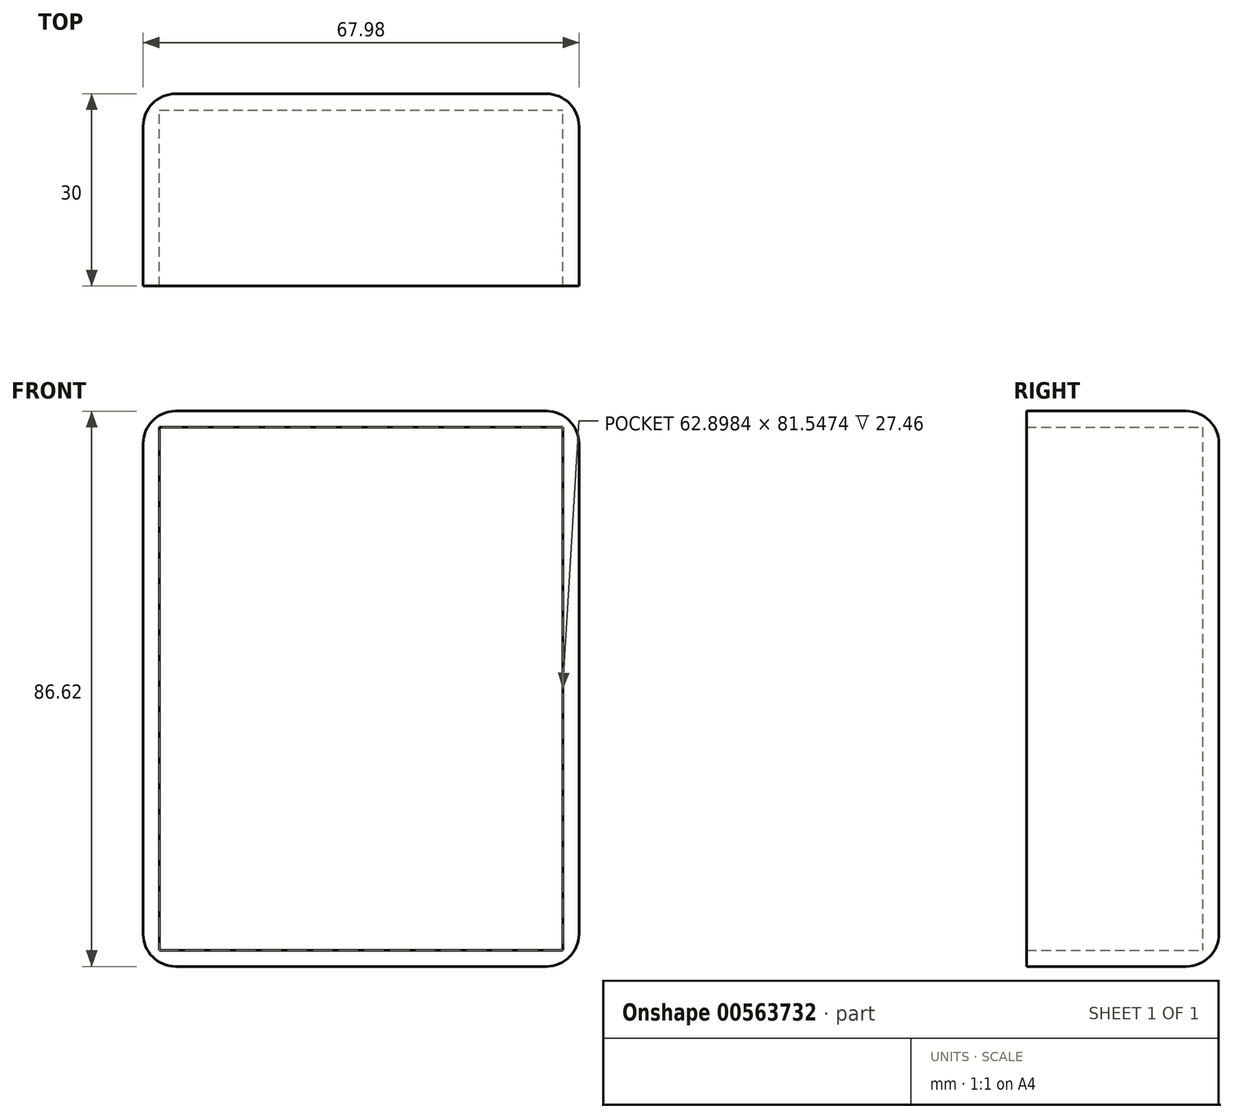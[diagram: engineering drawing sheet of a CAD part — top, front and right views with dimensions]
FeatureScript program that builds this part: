
annotation { "Feature Type Name" : "Feature", "Feature Type Description" : "" }
export const myFeature = defineFeature(function(context is Context, id is Id, definition is map)
    precondition{}
    {
        {
            var Q0;
            Q0=qCreatedBy(makeId("Front.planeOp"),FACE);
            var sketch = newSketch(context, id + "F0", { "sketchPlane" : qUnion([Q0])});
            skLineSegment(sketch, "E0.bottom", {"start": v(-33.99, 43.31) * mm, "end": v(33.99, 43.31) * mm});
            skLineSegment(sketch, "E0.top", {"start": v(-33.99, -43.31) * mm, "end": v(33.99, -43.31) * mm});
            skLineSegment(sketch, "E0.left", {"start": v(-33.99, 43.31) * mm, "end": v(-33.99, -43.31) * mm});
            skLineSegment(sketch, "E0.right", {"start": v(33.99, 43.31) * mm, "end": v(33.99, -43.31) * mm});
            skPoint(sketch, "E0.middle", {"position": v(0, 0) * mm});
            skLineSegment(sketch, "E1.bottom", {"start": v(141.07, -32.49) * mm, "end": v(165.13, -32.49) * mm});
            skLineSegment(sketch, "E1.top", {"start": v(141.07, -31.88) * mm, "end": v(165.13, -31.88) * mm});
            skLineSegment(sketch, "E1.left", {"start": v(141.07, -32.49) * mm, "end": v(141.07, -31.88) * mm});
            skLineSegment(sketch, "E1.right", {"start": v(165.13, -32.49) * mm, "end": v(165.13, -31.88) * mm});
            skPoint(sketch, "E1.middle", {"position": v(153.1, -32.18) * mm});
            skSolve(sketch);
        }
        {
            var Q0;
            Q0=makeQuery(id+"F0.imprint","IMPRINT",FACE,{"disambiguationData":[TD([[makeQuery(id+"F0.imprint","IMPRINT",EDGE,{"derivedFrom":sQuery(id+"F0.wireOp",EDGE,"E0.bottom")}),-1.0]])]});
            extrude(context, id + "F1", {"entities" : qUnion([Q0]), "depth" : 30 * mm, "offsetDistance" : 25.4 * mm});
        }
        {
            var Q0;
            Q0=makeQuery(id+"F1.opExtrude","CAP_FACE",FACE,{"disambiguationData":[OSD([sQuery(id+"F0.wireOp",EDGE,"E0.bottom"),sQuery(id+"F0.wireOp",EDGE,"E0.top"),sQuery(id+"F0.wireOp",EDGE,"E0.left"),sQuery(id+"F0.wireOp",EDGE,"E0.right")])],"isStart":false});
            shell(context, id + "F2", {"entities" : qUnion([Q0]), "thickness" : 2.54 * mm});
        }
        {
            var Q0;
            Q0=makeQuery(id+"F1.opExtrude","SWEPT_EDGE",EDGE,{"disambiguationData":[OSD([sQuery(id+"F0.wireOp",EDGE,"E0.bottom"),sQuery(id+"F0.wireOp",EDGE,"E0.left")])]});
            var Q1;
            Q1=makeQuery(id+"F1.opExtrude","CAP_EDGE",EDGE,{"disambiguationData":[OSD([sQuery(id+"F0.wireOp",EDGE,"E0.left")])],"isStart":true});
            var Q2;
            Q2=makeQuery(id+"F1.opExtrude","SWEPT_EDGE",EDGE,{"disambiguationData":[OSD([sQuery(id+"F0.wireOp",EDGE,"E0.bottom"),sQuery(id+"F0.wireOp",EDGE,"E0.right")])]});
            var Q3;
            Q3=makeQuery(id+"F1.opExtrude","CAP_EDGE",EDGE,{"disambiguationData":[OSD([sQuery(id+"F0.wireOp",EDGE,"E0.bottom")])],"isStart":true});
            var Q4;
            Q4=makeQuery(id+"F1.opExtrude","CAP_EDGE",EDGE,{"disambiguationData":[OSD([sQuery(id+"F0.wireOp",EDGE,"E0.right")])],"isStart":true});
            var Q5;
            Q5=makeQuery(id+"F1.opExtrude","CAP_EDGE",EDGE,{"disambiguationData":[OSD([sQuery(id+"F0.wireOp",EDGE,"E0.top")])],"isStart":true});
            var Q6;
            Q6=makeQuery(id+"F1.opExtrude","SWEPT_EDGE",EDGE,{"disambiguationData":[OSD([sQuery(id+"F0.wireOp",EDGE,"E0.top"),sQuery(id+"F0.wireOp",EDGE,"E0.right")])]});
            var Q7;
            Q7=makeQuery(id+"F1.opExtrude","SWEPT_EDGE",EDGE,{"disambiguationData":[OSD([sQuery(id+"F0.wireOp",EDGE,"E0.top"),sQuery(id+"F0.wireOp",EDGE,"E0.left")])]});
            var Q8;
            Q8=makeQuery(id+"F1.opExtrude","CAP_FACE",FACE,{"disambiguationData":[OSD([sQuery(id+"F0.wireOp",EDGE,"E0.bottom"),sQuery(id+"F0.wireOp",EDGE,"E0.top"),sQuery(id+"F0.wireOp",EDGE,"E0.left"),sQuery(id+"F0.wireOp",EDGE,"E0.right")])],"isStart":true});
            fillet(context, id + "F3", {"entities" : qUnion([Q0, Q1, Q2, Q3, Q4, Q5, Q6, Q7, Q8]), "radius" : 5.08 * mm, "tangentPropagation" : true, "allowEdgeOverflow" : false});
        }
    });
